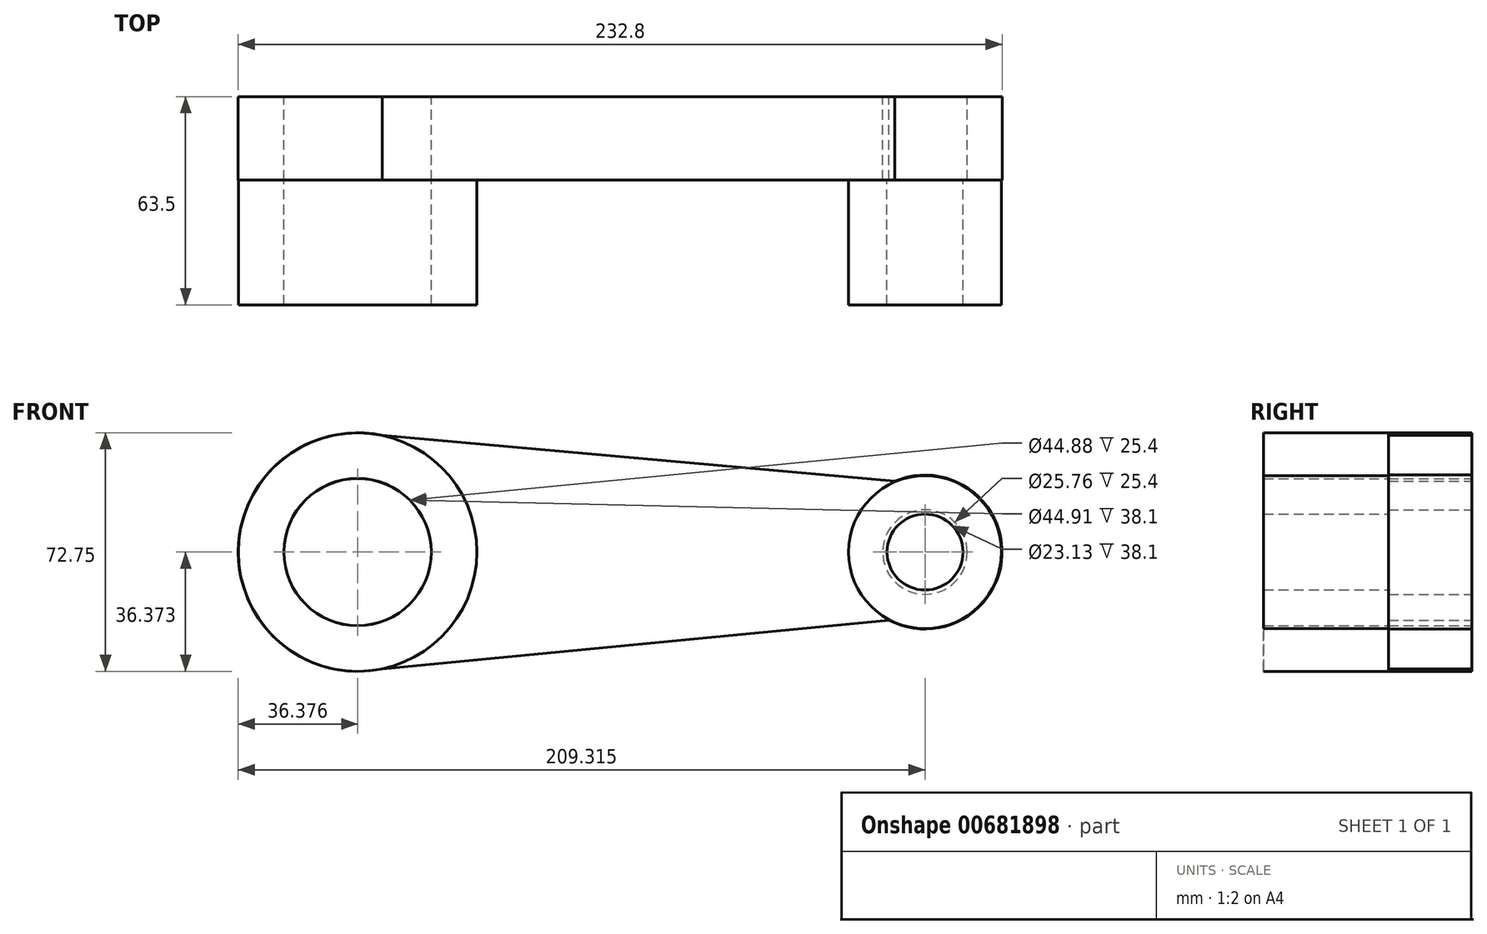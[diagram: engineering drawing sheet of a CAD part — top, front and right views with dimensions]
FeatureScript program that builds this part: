
annotation { "Feature Type Name" : "Feature", "Feature Type Description" : "" }
export const myFeature = defineFeature(function(context is Context, id is Id, definition is map)
    precondition{}
    {
        {
            var Q0;
            Q0=qCreatedBy(makeId("Front.planeOp"),FACE);
            var sketch = newSketch(context, id + "F0", { "sketchPlane" : qUnion([Q0])});
            skCircle(sketch, "E0", {"center": v(-94.98, 20.55) * mm, "radius": 36.38 * mm});
            skCircle(sketch, "E1", {"center": v(-94.98, 20.55) * mm, "radius": 22.44 * mm});
            skCircle(sketch, "E2", {"center": v(77.95, 20.55) * mm, "radius": 23.49 * mm});
            skCircle(sketch, "E3", {"center": v(77.95, 20.55) * mm, "radius": 12.88 * mm});
            skLineSegment(sketch, "E4", {"start": v(-87.47, 56.14) * mm, "end": v(68.73, 42.16) * mm});
            skLineSegment(sketch, "E5", {"start": v(-87.47, -15.04) * mm, "end": v(68.73, 0) * mm});
            skSolve(sketch);
        }
        {
            var Q0;
            Q0 = qSketchRegion(id + "F0", true);
            extrude(context, id + "F1", {"entities" : qUnion([Q0]), "depth" : 25.4 * mm, "offsetDistance" : 25.4 * mm});
        }
        {
            var Q0;
            Q0=makeQuery(id+"F1.opExtrude","CAP_FACE",FACE,{"disambiguationData":[OSD([sQuery(id+"F0.wireOp",EDGE,"E0"),sQuery(id+"F0.wireOp",EDGE,"E1"),sQuery(id+"F0.wireOp",EDGE,"E2"),sQuery(id+"F0.wireOp",EDGE,"E3"),sQuery(id+"F0.wireOp",EDGE,"E4"),sQuery(id+"F0.wireOp",EDGE,"E5")])],"isStart":false});
            var sketch = newSketch(context, id + "F2", { "sketchPlane" : qUnion([Q0])});
            skCircle(sketch, "E6", {"center": v(-94.98, 20.55) * mm, "radius": 36.35 * mm});
            skCircle(sketch, "E7", {"center": v(-94.98, 20.55) * mm, "radius": 22.46 * mm});
            skCircle(sketch, "E8", {"center": v(77.95, 20.55) * mm, "radius": 23.31 * mm});
            skCircle(sketch, "E9", {"center": v(77.95, 20.55) * mm, "radius": 11.57 * mm});
            skSolve(sketch);
        }
        {
            var Q0;
            Q0 = qSketchRegion(id + "F2", true);
            extrude(context, id + "F3", {"entities" : qUnion([Q0]), "operationType" : NewBodyOperationType.ADD, "depth" : 38.1 * mm, "offsetDistance" : 25.4 * mm});
        }
    });
